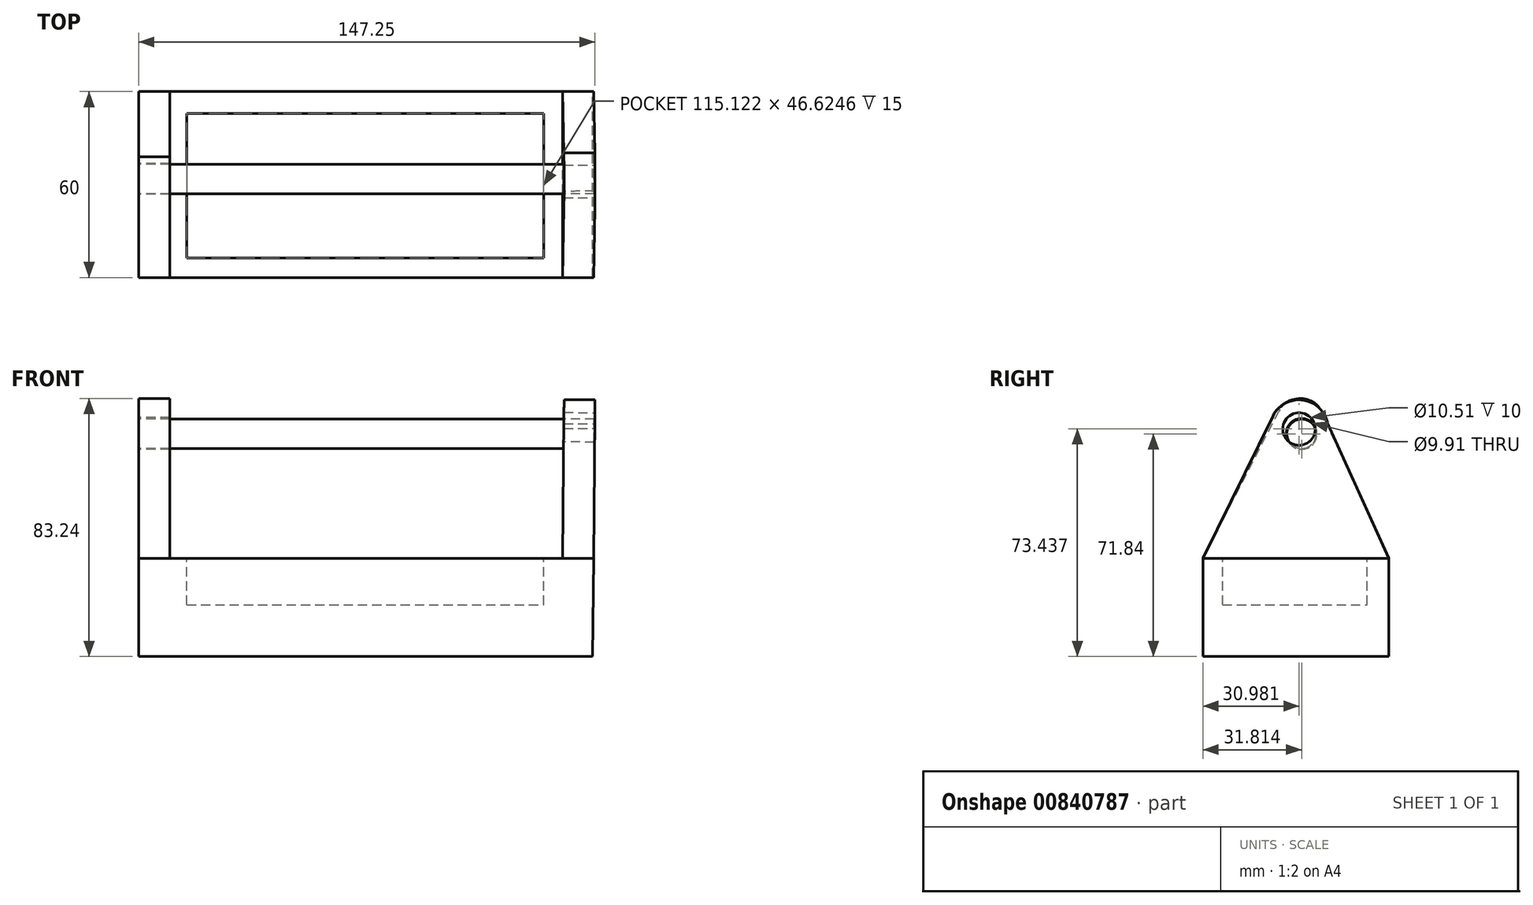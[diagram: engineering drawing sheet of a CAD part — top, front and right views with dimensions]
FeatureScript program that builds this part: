
annotation { "Feature Type Name" : "Feature", "Feature Type Description" : "" }
export const myFeature = defineFeature(function(context is Context, id is Id, definition is map)
    precondition{}
    {
        {
            var Q0;
            Q0=qCreatedBy(makeId("Front.planeOp"),FACE);
            var sketch = newSketch(context, id + "F0", { "sketchPlane" : qUnion([Q0])});
            skLineSegment(sketch, "E0", {"start": v(74.97, -15.1) * mm, "end": v(-71.8, -15.1) * mm});
            skLineSegment(sketch, "E1", {"start": v(-71.8, -15.1) * mm, "end": v(-71.8, -46.77) * mm});
            skLineSegment(sketch, "E2", {"start": v(-71.8, -46.77) * mm, "end": v(74.69, -46.77) * mm});
            skLineSegment(sketch, "E3", {"start": v(74.69, -46.77) * mm, "end": v(74.97, -15.1) * mm});
            skSolve(sketch);
        }
        {
            var Q0;
            Q0 = qSketchRegion(id + "F0", true);
            extrude(context, id + "F1", {"entities" : qUnion([Q0]), "depth" : 60 * mm, "offsetDistance" : 25 * mm});
        }
        {
            var Q0;
            Q0=makeQuery(id+"F1.opExtrude","SWEPT_FACE",FACE,{"disambiguationData":[OSD([sQuery(id+"F0.wireOp",EDGE,"E1")])]});
            var sketch = newSketch(context, id + "F2", { "sketchPlane" : qUnion([Q0])});
            skCircle(sketch, "E4", {"center": v(28.64, 28.64) * mm, "radius": 7.83 * mm});
            skLineSegment(sketch, "E5", {"start": v(0, -15.1) * mm, "end": v(22.4, 33.37) * mm});
            skLineSegment(sketch, "E6", {"start": v(0, -15.1) * mm, "end": v(60, -15.1) * mm});
            skLineSegment(sketch, "E7", {"start": v(60, -15.1) * mm, "end": v(35.6, 32.22) * mm});
            skSolve(sketch);
        }
        {
            var Q0;
            Q0 = qSketchRegion(id + "F2", true);
            extrude(context, id + "F3", {"entities" : qUnion([Q0]), "operationType" : NewBodyOperationType.ADD, "oppositeDirection" : true, "depth" : 10 * mm, "offsetDistance" : 25 * mm});
        }
        {
            var Q0;
            Q0=makeQuery(id+"F1.opExtrude","SWEPT_FACE",FACE,{"disambiguationData":[OSD([sQuery(id+"F0.wireOp",EDGE,"E3")])]});
            var sketch = newSketch(context, id + "F4", { "sketchPlane" : qUnion([Q0])});
            skCircle(sketch, "E8", {"center": v(-29.02, 27.3) * mm, "radius": 9.4 * mm});
            skLineSegment(sketch, "E9", {"start": v(-60, -14.43) * mm, "end": v(-37.45, 31.45) * mm});
            skLineSegment(sketch, "E10", {"start": v(-60, -14.43) * mm, "end": v(0, -14.43) * mm});
            skLineSegment(sketch, "E11", {"start": v(0, -14.43) * mm, "end": v(-19.77, 28.96) * mm});
            skSolve(sketch);
        }
        {
            var Q0;
            Q0 = qSketchRegion(id + "F4", true);
            extrude(context, id + "F5", {"entities" : qUnion([Q0]), "oppositeDirection" : true, "depth" : 10 * mm, "offsetDistance" : 25 * mm});
        }
        {
            var Q0;
            Q0=makeQuery(id+"F1.opExtrude","SWEPT_FACE",FACE,{"disambiguationData":[OSD([sQuery(id+"F0.wireOp",EDGE,"E0")])]});
            var sketch = newSketch(context, id + "F6", { "sketchPlane" : qUnion([Q0])});
            skLineSegment(sketch, "E12", {"start": v(58.83, -53.96) * mm, "end": v(58.83, -7.05) * mm});
            skLineSegment(sketch, "E13", {"start": v(58.83, -7.05) * mm, "end": v(-56.3, -7.05) * mm});
            skLineSegment(sketch, "E14", {"start": v(-56.3, -7.05) * mm, "end": v(-56.3, -53.68) * mm});
            skLineSegment(sketch, "E15", {"start": v(-56.3, -53.68) * mm, "end": v(58.83, -53.68) * mm});
            skSolve(sketch);
        }
        {
            var Q0;
            Q0 = qSketchRegion(id + "F6", true);
            extrude(context, id + "F7", {"entities" : qUnion([Q0]), "operationType" : NewBodyOperationType.REMOVE, "oppositeDirection" : true, "depth" : 15 * mm, "offsetDistance" : 25 * mm});
        }
        {
            var Q0;
            Q0=makeQuery(id+"F3.boolean.opBoolean","MERGE",FACE,{"derivedFrom":[makeQuery(id+"F1.opExtrude","SWEPT_FACE",FACE,{"disambiguationData":[OSD([sQuery(id+"F0.wireOp",EDGE,"E1")])]}),makeQuery(id+"F3.opExtrude","CAP_FACE",FACE,{"disambiguationData":[OSD([sQuery(id+"F2.wireOp",EDGE,"E4"),sQuery(id+"F2.wireOp",EDGE,"E5"),sQuery(id+"F2.wireOp",EDGE,"E6"),sQuery(id+"F2.wireOp",EDGE,"E7")])],"isStart":true})]});
            var sketch = newSketch(context, id + "F8", { "sketchPlane" : qUnion([Q0])});
            skCircle(sketch, "E16", {"center": v(28.19, 25.07) * mm, "radius": 4.96 * mm});
            skSolve(sketch);
        }
        {
            var Q0;
            Q0 = qSketchRegion(id + "F8", true);
            extrude(context, id + "F9", {"entities" : qUnion([Q0]), "operationType" : NewBodyOperationType.REMOVE, "oppositeDirection" : true, "depth" : 25 * mm, "offsetDistance" : 25 * mm});
        }
        {
            var Q0;
            Q0=makeQuery(id+"F5.opExtrude","CAP_FACE",FACE,{"disambiguationData":[OSD([sQuery(id+"F4.wireOp",EDGE,"E8"),sQuery(id+"F4.wireOp",EDGE,"E9"),sQuery(id+"F4.wireOp",EDGE,"E10"),sQuery(id+"F4.wireOp",EDGE,"E11")])],"isStart":true});
            var sketch = newSketch(context, id + "F10", { "sketchPlane" : qUnion([Q0])});
            skCircle(sketch, "E17", {"center": v(-29.02, 27.3) * mm, "radius": 5.25 * mm});
            skSolve(sketch);
        }
        {
            var Q0;
            Q0 = qSketchRegion(id + "F10", true);
            extrude(context, id + "F11", {"entities" : qUnion([Q0]), "operationType" : NewBodyOperationType.REMOVE, "oppositeDirection" : true, "depth" : 25 * mm, "offsetDistance" : 25 * mm});
        }
        {
            var Q0;
            Q0=makeQuery(id+"F3.boolean.opBoolean","MERGE",FACE,{"derivedFrom":[makeQuery(id+"F1.opExtrude","SWEPT_FACE",FACE,{"disambiguationData":[OSD([sQuery(id+"F0.wireOp",EDGE,"E1")])]}),makeQuery(id+"F3.opExtrude","CAP_FACE",FACE,{"disambiguationData":[OSD([sQuery(id+"F2.wireOp",EDGE,"E4"),sQuery(id+"F2.wireOp",EDGE,"E5"),sQuery(id+"F2.wireOp",EDGE,"E6"),sQuery(id+"F2.wireOp",EDGE,"E7")])],"isStart":true})]});
            var sketch = newSketch(context, id + "F12", { "sketchPlane" : qUnion([Q0])});
            skCircle(sketch, "E18", {"center": v(28.19, 25.07) * mm, "radius": 4.75 * mm});
            skSolve(sketch);
        }
        {
            var Q0;
            Q0 = qSketchRegion(id + "F12", true);
            extrude(context, id + "F13", {"entities" : qUnion([Q0]), "operationType" : NewBodyOperationType.ADD, "oppositeDirection" : true, "depth" : 147 * mm, "offsetDistance" : 25 * mm});
        }
    });
